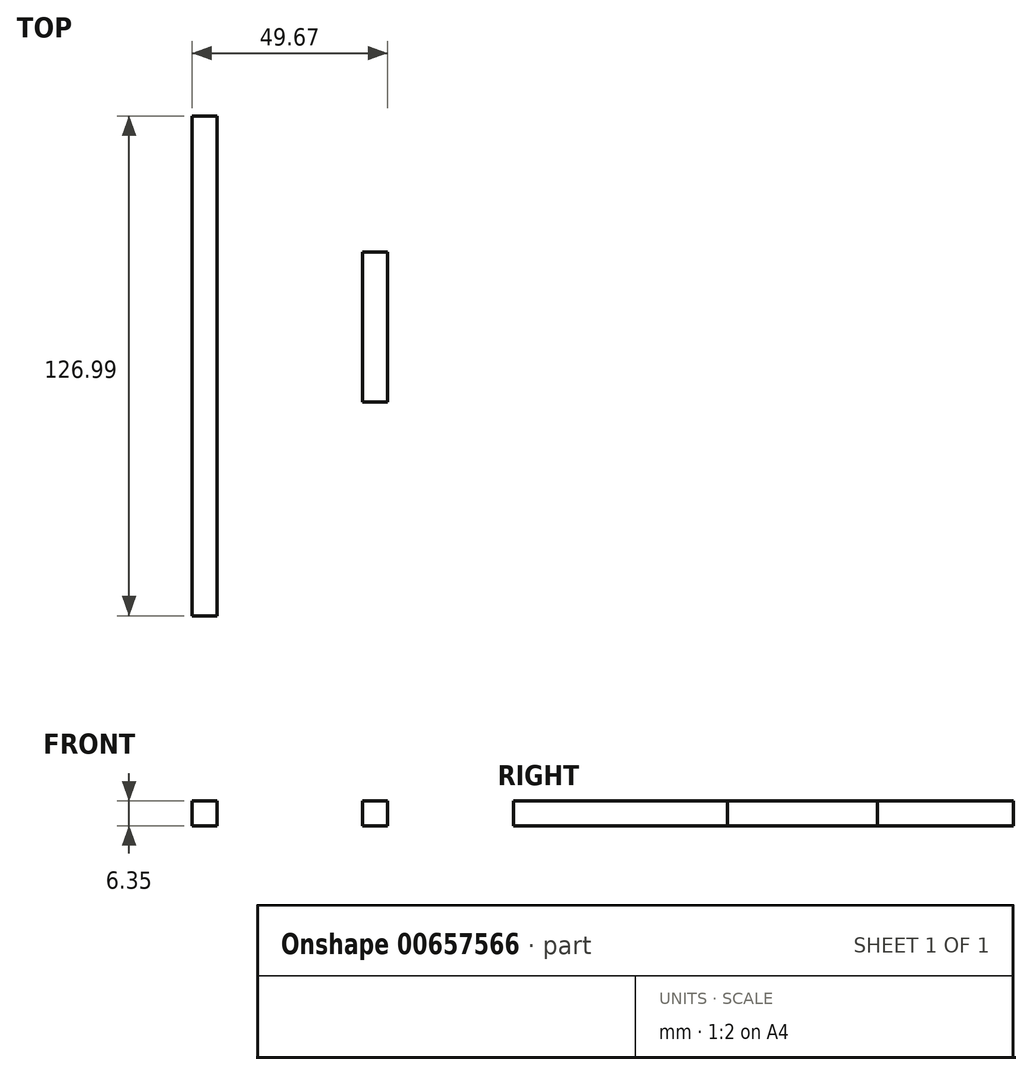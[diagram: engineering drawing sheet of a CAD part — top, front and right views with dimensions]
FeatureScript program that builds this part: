
annotation { "Feature Type Name" : "Feature", "Feature Type Description" : "" }
export const myFeature = defineFeature(function(context is Context, id is Id, definition is map)
    precondition{}
    {
        {
            var Q0;
            Q0=qCreatedBy(makeId("Top.planeOp"),FACE);
            var sketch = newSketch(context, id + "F0", { "sketchPlane" : qUnion([Q0])});
            skLineSegment(sketch, "E0.bottom", {"start": v(-89.46, 69.5) * mm, "end": v(-83.06, 69.5) * mm});
            skLineSegment(sketch, "E0.top", {"start": v(-89.46, -57.5) * mm, "end": v(-83.06, -57.5) * mm});
            skLineSegment(sketch, "E0.left", {"start": v(-89.46, 69.5) * mm, "end": v(-89.46, -57.5) * mm});
            skLineSegment(sketch, "E0.right", {"start": v(-83.06, 69.5) * mm, "end": v(-83.06, -57.5) * mm});
            skSolve(sketch);
        }
        {
            var Q0;
            Q0 = qSketchRegion(id + "F0", true);
            extrude(context, id + "F1", {"entities" : qUnion([Q0]), "depth" : 6.35 * mm, "offsetDistance" : 25.4 * mm});
        }
        {
            var Q0;
            Q0=qCreatedBy(makeId("Top.planeOp"),FACE);
            var sketch = newSketch(context, id + "F2", { "sketchPlane" : qUnion([Q0])});
            skLineSegment(sketch, "E1.bottom", {"start": v(-46.14, 34.9) * mm, "end": v(-39.79, 34.9) * mm});
            skLineSegment(sketch, "E1.top", {"start": v(-46.14, -3.2) * mm, "end": v(-39.79, -3.2) * mm});
            skLineSegment(sketch, "E1.left", {"start": v(-46.14, -3.2) * mm, "end": v(-46.14, 34.9) * mm});
            skLineSegment(sketch, "E1.right", {"start": v(-39.79, -3.2) * mm, "end": v(-39.79, 34.9) * mm});
            skSolve(sketch);
        }
        {
            var Q0;
            Q0=makeQuery(id+"F2.imprint","IMPRINT",FACE,{"disambiguationData":[TD([[makeQuery(id+"F2.imprint","IMPRINT",EDGE,{"derivedFrom":sQuery(id+"F2.wireOp",EDGE,"E1.bottom")}),-1.0]])]});
            extrude(context, id + "F3", {"entities" : qUnion([Q0]), "depth" : 6.35 * mm, "offsetDistance" : 25.4 * mm});
        }
    });
